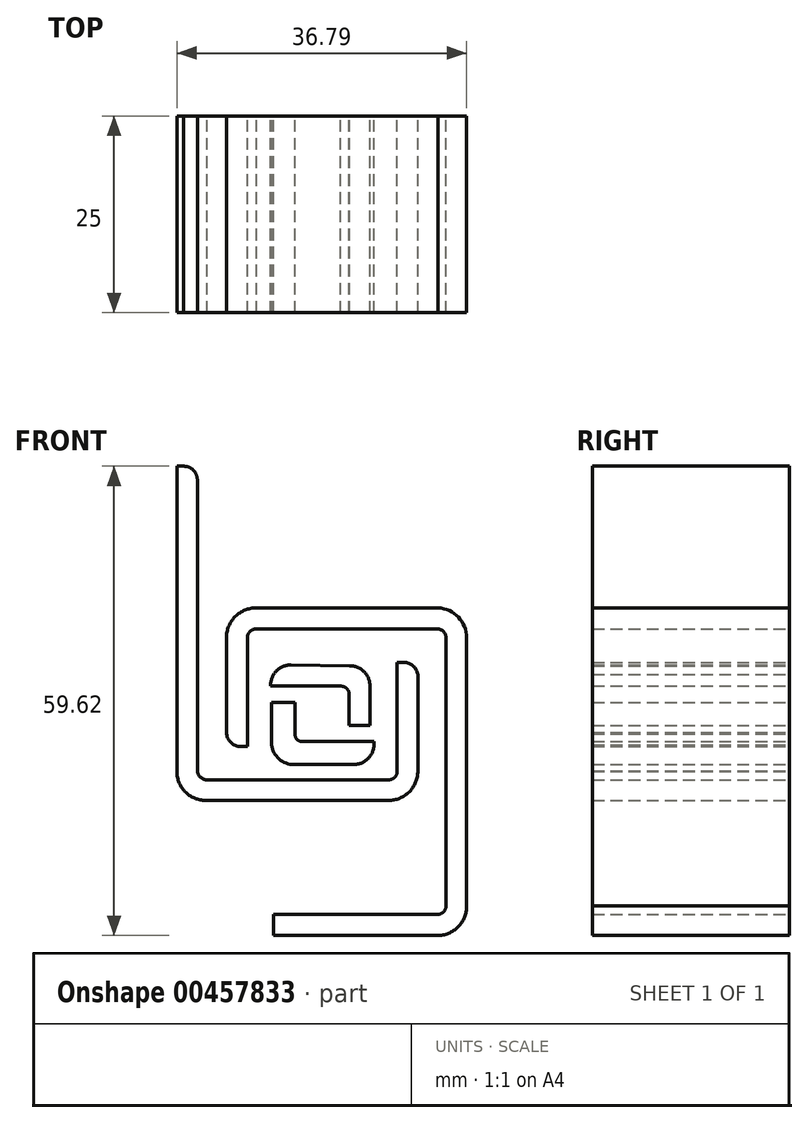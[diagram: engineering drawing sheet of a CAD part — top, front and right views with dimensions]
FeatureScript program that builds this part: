
annotation { "Feature Type Name" : "Feature", "Feature Type Description" : "" }
export const myFeature = defineFeature(function(context is Context, id is Id, definition is map)
    precondition{}
    {
        {
            var Q0;
            Q0=qCreatedBy(makeId("Front.planeOp"),FACE);
            var sketch = newSketch(context, id + "F0", { "sketchPlane" : qUnion([Q0])});
            skLineSegment(sketch, "E0", {"start": v(-45.22, 106.22) * mm, "end": v(-45.22, 67.43) * mm});
            skLineSegment(sketch, "E1", {"start": v(-41.38, 63.76) * mm, "end": v(-18.35, 63.76) * mm});
            skLineSegment(sketch, "E2", {"start": v(-18.35, 66.37) * mm, "end": v(-41.34, 66.37) * mm});
            skLineSegment(sketch, "E3", {"start": v(-44.37, 106.22) * mm, "end": v(-45.22, 106.22) * mm});
            skLineSegment(sketch, "E4", {"start": v(-42.62, 67.42) * mm, "end": v(-42.62, 104.5) * mm});
            skArc(sketch, "E5", {"start": v(-42.62, 104.5) * mm, "mid": v(-43.14, 105.73) * mm, "end": v(-44.37, 106.22) * mm});
            skArc(sketch, "E6", {"start": v(-45.22, 67.43) * mm, "mid": v(-44.09, 64.77) * mm, "end": v(-41.38, 63.76) * mm});
            skArc(sketch, "E7", {"start": v(-41.34, 66.37) * mm, "mid": v(-42.17, 66.67) * mm, "end": v(-42.62, 67.42) * mm});
            skArc(sketch, "E8", {"start": v(-18.35, 66.37) * mm, "mid": v(-17.55, 66.71) * mm, "end": v(-17.24, 67.53) * mm});
            skArc(sketch, "E9", {"start": v(-18.35, 63.76) * mm, "mid": v(-15.7, 64.87) * mm, "end": v(-14.62, 67.53) * mm});
            skLineSegment(sketch, "E10", {"start": v(-14.62, 67.53) * mm, "end": v(-14.62, 79.76) * mm});
            skLineSegment(sketch, "E11", {"start": v(-17.24, 67.53) * mm, "end": v(-17.24, 81.3) * mm});
            skLineSegment(sketch, "E12", {"start": v(-17.24, 81.3) * mm, "end": v(-16.38, 81.3) * mm});
            skArc(sketch, "E13", {"start": v(-16.38, 81.3) * mm, "mid": v(-15.21, 80.86) * mm, "end": v(-14.62, 79.76) * mm});
            skSolve(sketch);
        }
        {
            var Q0;
            Q0=makeQuery(id+"F0.imprint","IMPRINT",FACE,{"disambiguationData":[TD([[makeQuery(id+"F0.imprint","IMPRINT",EDGE,{"derivedFrom":sQuery(id+"F0.wireOp",EDGE,"E0")}),1.0]])]});
            extrude(context, id + "F1", {"entities" : qUnion([Q0]), "depth" : 25 * mm});
        }
        {
            var Q0;
            Q0=qCreatedBy(makeId("Front.planeOp"),FACE);
            var sketch = newSketch(context, id + "F2", { "sketchPlane" : qUnion([Q0])});
            skLineSegment(sketch, "E14", {"start": v(-6.1, -25.26) * mm, "end": v(-3.1, -25.26) * mm});
            skLineSegment(sketch, "E15", {"start": v(-3.1, -25.26) * mm, "end": v(-3.1, -29.3) * mm});
            skLineSegment(sketch, "E16", {"start": v(-6.1, -25.26) * mm, "end": v(-6.1, -30.67) * mm});
            skLineSegment(sketch, "E17", {"start": v(-2.24, -30.26) * mm, "end": v(6.9, -30.26) * mm});
            skArc(sketch, "E18", {"start": v(-3.22, -33.18) * mm, "mid": v(-5.13, -32.47) * mm, "end": v(-6.1, -30.67) * mm});
            skArc(sketch, "E19", {"start": v(-2.24, -30.26) * mm, "mid": v(-2.88, -29.97) * mm, "end": v(-3.1, -29.3) * mm});
            skLineSegment(sketch, "E20", {"start": v(4.3, -33.18) * mm, "end": v(-3.22, -33.18) * mm});
            skArc(sketch, "E21", {"start": v(4.3, -33.18) * mm, "mid": v(6.26, -32.3) * mm, "end": v(6.9, -30.26) * mm});
            skSolve(sketch);
        }
        {
            var Q0;
            Q0=makeQuery(id+"F2.imprint","IMPRINT",FACE,{"disambiguationData":[TD([[makeQuery(id+"F2.imprint","IMPRINT",EDGE,{"derivedFrom":sQuery(id+"F2.wireOp",EDGE,"E14")}),-1.0]])]});
            extrude(context, id + "F3", {"entities" : qUnion([Q0]), "depth" : 25 * mm});
        }
        {
            var Q0;
            Q0=qCreatedBy(makeId("Front.planeOp"),FACE);
            var sketch = newSketch(context, id + "F4", { "sketchPlane" : qUnion([Q0])});
            skLineSegment(sketch, "E22", {"start": v(-6.2, 22.48) * mm, "end": v(2.65, 22.48) * mm});
            skLineSegment(sketch, "E23", {"start": v(3.77, 17.52) * mm, "end": v(6.4, 17.52) * mm});
            skLineSegment(sketch, "E24", {"start": v(6.4, 17.52) * mm, "end": v(6.4, 22.53) * mm});
            skLineSegment(sketch, "E25", {"start": v(3.84, 25.08) * mm, "end": v(-3.63, 25.17) * mm});
            skArc(sketch, "E26", {"start": v(-3.63, 25.17) * mm, "mid": v(-5.5, 24.39) * mm, "end": v(-6.2, 22.48) * mm});
            skArc(sketch, "E27", {"start": v(6.4, 22.53) * mm, "mid": v(5.64, 24.34) * mm, "end": v(3.84, 25.08) * mm});
            skLineSegment(sketch, "E28", {"start": v(3.77, 21.45) * mm, "end": v(3.77, 17.52) * mm});
            skArc(sketch, "E29", {"start": v(3.77, 21.45) * mm, "mid": v(3.44, 22.21) * mm, "end": v(2.65, 22.48) * mm});
            skSolve(sketch);
        }
        {
            var Q0;
            Q0=makeQuery(id+"F4.imprint","IMPRINT",FACE,{"disambiguationData":[TD([[makeQuery(id+"F4.imprint","IMPRINT",EDGE,{"derivedFrom":sQuery(id+"F4.wireOp",EDGE,"E22")}),1.0]])]});
            extrude(context, id + "F5", {"entities" : qUnion([Q0]), "depth" : 25 * mm});
        }
        {
            var Q0;
            Q0=qCreatedBy(makeId("Front.planeOp"),FACE);
            var sketch = newSketch(context, id + "F6", { "sketchPlane" : qUnion([Q0])});
            skLineSegment(sketch, "E30", {"start": v(16.83, -86.4) * mm, "end": v(16.83, -72.58) * mm});
            skLineSegment(sketch, "E31", {"start": v(20.15, -107.72) * mm, "end": v(20.15, -110.4) * mm});
            skLineSegment(sketch, "E32", {"start": v(20.15, -110.4) * mm, "end": v(40.96, -110.4) * mm});
            skLineSegment(sketch, "E33", {"start": v(16.01, -86.4) * mm, "end": v(16.83, -86.4) * mm});
            skPoint(sketch, "E34.end.orphan", {"position": v(14.17, -86.4) * mm});
            skArc(sketch, "E35", {"start": v(16.01, -86.4) * mm, "mid": v(14.73, -85.88) * mm, "end": v(14.17, -84.61) * mm});
            skLineSegment(sketch, "E36", {"start": v(17.99, -71.44) * mm, "end": v(40.98, -71.44) * mm});
            skLineSegment(sketch, "E37", {"start": v(14.17, -72.57) * mm, "end": v(14.17, -84.61) * mm});
            skArc(sketch, "E38", {"start": v(16.83, -72.58) * mm, "mid": v(17.17, -71.77) * mm, "end": v(17.99, -71.44) * mm});
            skArc(sketch, "E39", {"start": v(14.17, -72.57) * mm, "mid": v(15.3, -69.88) * mm, "end": v(17.99, -68.77) * mm});
            skLineSegment(sketch, "E40", {"start": v(42.06, -72.58) * mm, "end": v(42.06, -106.55) * mm});
            skLineSegment(sketch, "E41", {"start": v(41.06, -68.77) * mm, "end": v(17.99, -68.77) * mm});
            skArc(sketch, "E42", {"start": v(42.06, -72.58) * mm, "mid": v(41.75, -71.8) * mm, "end": v(40.98, -71.44) * mm});
            skArc(sketch, "E43", {"start": v(44.67, -72.58) * mm, "mid": v(43.63, -69.95) * mm, "end": v(41.06, -68.77) * mm});
            skLineSegment(sketch, "E44", {"start": v(44.67, -106.64) * mm, "end": v(44.67, -72.58) * mm});
            skLineSegment(sketch, "E45", {"start": v(40.98, -107.72) * mm, "end": v(20.15, -107.72) * mm});
            skArc(sketch, "E46", {"start": v(40.98, -107.72) * mm, "mid": v(41.78, -107.37) * mm, "end": v(42.06, -106.55) * mm});
            skArc(sketch, "E47", {"start": v(40.96, -110.4) * mm, "mid": v(43.6, -109.3) * mm, "end": v(44.67, -106.64) * mm});
            skSolve(sketch);
        }
        {
            var Q0;
            Q0=makeQuery(id+"F6.imprint","IMPRINT",FACE,{"disambiguationData":[TD([[makeQuery(id+"F6.imprint","IMPRINT",EDGE,{"derivedFrom":sQuery(id+"F6.wireOp",EDGE,"E30")}),1.0]])]});
            extrude(context, id + "F7", {"entities" : qUnion([Q0]), "depth" : 25 * mm});
        }
        {
            var Q0;
            Q0=makeQuery(id+"F1.opExtrude","SWEPT_BODY",BODY,{"disambiguationData":[OSD([sQuery(id+"F0.wireOp",EDGE,"E0"),sQuery(id+"F0.wireOp",EDGE,"E1"),sQuery(id+"F0.wireOp",EDGE,"E2"),sQuery(id+"F0.wireOp",EDGE,"E3"),sQuery(id+"F0.wireOp",EDGE,"E4"),sQuery(id+"F0.wireOp",EDGE,"E5"),sQuery(id+"F0.wireOp",EDGE,"E6"),sQuery(id+"F0.wireOp",EDGE,"E7"),sQuery(id+"F0.wireOp",EDGE,"E9"),sQuery(id+"F0.wireOp",EDGE,"E10"),sQuery(id+"F0.wireOp",EDGE,"E11"),sQuery(id+"F0.wireOp",EDGE,"E12"),sQuery(id+"F0.wireOp",EDGE,"E13"),sQuery(id+"F0.wireOp",EDGE,"E8")])]});
            transform(context, id + "F8", {"entities" : qUnion([Q0]), "transformType" : TransformType.TRANSLATION_3D, "dx" : 29 * mm, "dy" : 0 * mm, "dz" : -77 * mm, "makeCopy" : true});
        }
        {
            var Q0;
            Q0=makeQuery(id+"F3.opExtrude","SWEPT_BODY",BODY,{"disambiguationData":[OSD([sQuery(id+"F2.wireOp",EDGE,"E14"),sQuery(id+"F2.wireOp",EDGE,"E15"),sQuery(id+"F2.wireOp",EDGE,"E16"),sQuery(id+"F2.wireOp",EDGE,"E17"),sQuery(id+"F2.wireOp",EDGE,"E18"),sQuery(id+"F2.wireOp",EDGE,"E19"),sQuery(id+"F2.wireOp",EDGE,"E20"),sQuery(id+"F2.wireOp",EDGE,"E21")])]});
            transform(context, id + "F9", {"entities" : qUnion([Q0]), "transformType" : TransformType.TRANSLATION_3D, "dx" : 0 * mm, "dy" : 0 * mm, "dz" : 24.5 * mm, "makeCopy" : true});
        }
        {
            var Q0;
            Q0=makeQuery(id+"F5.opExtrude","SWEPT_BODY",BODY,{"disambiguationData":[OSD([sQuery(id+"F4.wireOp",EDGE,"E22"),sQuery(id+"F4.wireOp",EDGE,"E23"),sQuery(id+"F4.wireOp",EDGE,"E24"),sQuery(id+"F4.wireOp",EDGE,"E25"),sQuery(id+"F4.wireOp",EDGE,"E26"),sQuery(id+"F4.wireOp",EDGE,"E27"),sQuery(id+"F4.wireOp",EDGE,"E28"),sQuery(id+"F4.wireOp",EDGE,"E29")])]});
            transform(context, id + "F10", {"entities" : qUnion([Q0]), "transformType" : TransformType.TRANSLATION_3D, "dx" : 0 * mm, "dy" : 0 * mm, "dz" : -21.2 * mm, "makeCopy" : true});
        }
        {
            var Q0;
            Q0=makeQuery(id+"F7.opExtrude","SWEPT_BODY",BODY,{"disambiguationData":[OSD([sQuery(id+"F6.wireOp",EDGE,"E30"),sQuery(id+"F6.wireOp",EDGE,"E31"),sQuery(id+"F6.wireOp",EDGE,"E32"),sQuery(id+"F6.wireOp",EDGE,"E33"),sQuery(id+"F6.wireOp",EDGE,"E35"),sQuery(id+"F6.wireOp",EDGE,"E36"),sQuery(id+"F6.wireOp",EDGE,"E37"),sQuery(id+"F6.wireOp",EDGE,"E38"),sQuery(id+"F6.wireOp",EDGE,"E39"),sQuery(id+"F6.wireOp",EDGE,"E40"),sQuery(id+"F6.wireOp",EDGE,"E41"),sQuery(id+"F6.wireOp",EDGE,"E42"),sQuery(id+"F6.wireOp",EDGE,"E43"),sQuery(id+"F6.wireOp",EDGE,"E44"),sQuery(id+"F6.wireOp",EDGE,"E45"),sQuery(id+"F6.wireOp",EDGE,"E46"),sQuery(id+"F6.wireOp",EDGE,"E47")])]});
            transform(context, id + "F11", {"entities" : qUnion([Q0]), "transformType" : TransformType.TRANSLATION_3D, "dx" : -26 * mm, "dy" : 0 * mm, "dz" : 80 * mm, "makeCopy" : true});
        }
        {
            var Q0;
            Q0=makeQuery(id+"F1.opExtrude","SWEPT_BODY",BODY,{"disambiguationData":[OSD([sQuery(id+"F0.wireOp",EDGE,"E0"),sQuery(id+"F0.wireOp",EDGE,"E1"),sQuery(id+"F0.wireOp",EDGE,"E2"),sQuery(id+"F0.wireOp",EDGE,"E3"),sQuery(id+"F0.wireOp",EDGE,"E4"),sQuery(id+"F0.wireOp",EDGE,"E5"),sQuery(id+"F0.wireOp",EDGE,"E6"),sQuery(id+"F0.wireOp",EDGE,"E7"),sQuery(id+"F0.wireOp",EDGE,"E9"),sQuery(id+"F0.wireOp",EDGE,"E10"),sQuery(id+"F0.wireOp",EDGE,"E11"),sQuery(id+"F0.wireOp",EDGE,"E12"),sQuery(id+"F0.wireOp",EDGE,"E13"),sQuery(id+"F0.wireOp",EDGE,"E8")])]});
            var Q1;
            Q1=makeQuery(id+"F5.opExtrude","SWEPT_BODY",BODY,{"disambiguationData":[OSD([sQuery(id+"F4.wireOp",EDGE,"E22"),sQuery(id+"F4.wireOp",EDGE,"E23"),sQuery(id+"F4.wireOp",EDGE,"E24"),sQuery(id+"F4.wireOp",EDGE,"E25"),sQuery(id+"F4.wireOp",EDGE,"E26"),sQuery(id+"F4.wireOp",EDGE,"E27"),sQuery(id+"F4.wireOp",EDGE,"E28"),sQuery(id+"F4.wireOp",EDGE,"E29")])]});
            deleteBodies(context, id + "F12", {"entities" : qUnion([Q0, Q1])});
        }
        {
            var Q0;
            Q0=makeQuery(id+"F7.opExtrude","SWEPT_BODY",BODY,{"disambiguationData":[OSD([sQuery(id+"F6.wireOp",EDGE,"E30"),sQuery(id+"F6.wireOp",EDGE,"E31"),sQuery(id+"F6.wireOp",EDGE,"E32"),sQuery(id+"F6.wireOp",EDGE,"E33"),sQuery(id+"F6.wireOp",EDGE,"E35"),sQuery(id+"F6.wireOp",EDGE,"E36"),sQuery(id+"F6.wireOp",EDGE,"E37"),sQuery(id+"F6.wireOp",EDGE,"E38"),sQuery(id+"F6.wireOp",EDGE,"E39"),sQuery(id+"F6.wireOp",EDGE,"E40"),sQuery(id+"F6.wireOp",EDGE,"E41"),sQuery(id+"F6.wireOp",EDGE,"E42"),sQuery(id+"F6.wireOp",EDGE,"E43"),sQuery(id+"F6.wireOp",EDGE,"E44"),sQuery(id+"F6.wireOp",EDGE,"E45"),sQuery(id+"F6.wireOp",EDGE,"E46"),sQuery(id+"F6.wireOp",EDGE,"E47")])]});
            deleteBodies(context, id + "F13", {"entities" : qUnion([Q0])});
        }
        {
            var Q0;
            Q0=makeQuery(id+"F3.opExtrude","SWEPT_BODY",BODY,{"disambiguationData":[OSD([sQuery(id+"F2.wireOp",EDGE,"E14"),sQuery(id+"F2.wireOp",EDGE,"E15"),sQuery(id+"F2.wireOp",EDGE,"E16"),sQuery(id+"F2.wireOp",EDGE,"E17"),sQuery(id+"F2.wireOp",EDGE,"E18"),sQuery(id+"F2.wireOp",EDGE,"E19"),sQuery(id+"F2.wireOp",EDGE,"E20"),sQuery(id+"F2.wireOp",EDGE,"E21")])]});
            deleteBodies(context, id + "F14", {"entities" : qUnion([Q0])});
        }
        {
            var Q0;
            Q0=makeQuery(id+"F8.opPattern","COPY",BODY,{"derivedFrom":makeQuery(id+"F1.opExtrude","SWEPT_BODY",BODY,{"disambiguationData":[OSD([sQuery(id+"F0.wireOp",EDGE,"E0"),sQuery(id+"F0.wireOp",EDGE,"E1"),sQuery(id+"F0.wireOp",EDGE,"E2"),sQuery(id+"F0.wireOp",EDGE,"E3"),sQuery(id+"F0.wireOp",EDGE,"E4"),sQuery(id+"F0.wireOp",EDGE,"E5"),sQuery(id+"F0.wireOp",EDGE,"E6"),sQuery(id+"F0.wireOp",EDGE,"E7"),sQuery(id+"F0.wireOp",EDGE,"E9"),sQuery(id+"F0.wireOp",EDGE,"E10"),sQuery(id+"F0.wireOp",EDGE,"E11"),sQuery(id+"F0.wireOp",EDGE,"E12"),sQuery(id+"F0.wireOp",EDGE,"E13"),sQuery(id+"F0.wireOp",EDGE,"E8")])]}),"instanceName":"1"});
            transform(context, id + "F15", {"entities" : qUnion([Q0]), "transformType" : TransformType.TRANSLATION_3D, "dx" : -1.9 * mm, "dy" : 0 * mm, "dz" : 0 * mm, "makeCopy" : true});
        }
        {
            var Q0;
            Q0=makeQuery(id+"F8.opPattern","COPY",BODY,{"derivedFrom":makeQuery(id+"F1.opExtrude","SWEPT_BODY",BODY,{"disambiguationData":[OSD([sQuery(id+"F0.wireOp",EDGE,"E0"),sQuery(id+"F0.wireOp",EDGE,"E1"),sQuery(id+"F0.wireOp",EDGE,"E2"),sQuery(id+"F0.wireOp",EDGE,"E3"),sQuery(id+"F0.wireOp",EDGE,"E4"),sQuery(id+"F0.wireOp",EDGE,"E5"),sQuery(id+"F0.wireOp",EDGE,"E6"),sQuery(id+"F0.wireOp",EDGE,"E7"),sQuery(id+"F0.wireOp",EDGE,"E9"),sQuery(id+"F0.wireOp",EDGE,"E10"),sQuery(id+"F0.wireOp",EDGE,"E11"),sQuery(id+"F0.wireOp",EDGE,"E12"),sQuery(id+"F0.wireOp",EDGE,"E13"),sQuery(id+"F0.wireOp",EDGE,"E8")])]}),"instanceName":"1"});
            deleteBodies(context, id + "F16", {"entities" : qUnion([Q0])});
        }
    });
